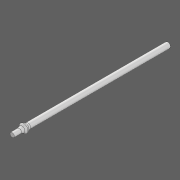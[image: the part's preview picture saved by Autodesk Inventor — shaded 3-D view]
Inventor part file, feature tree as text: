
AUTODESK INVENTOR PART (.ipt)
format: ipt  version: 2020 (Build 240168000, 168)  size: 101,888 bytes
history: native  units: in
note: dims shown in document units (in); Inventor stores cm internally (conversion verified against a paired STEP export)
features: revolve x1, fillet x1, sketch x1
ambient origin geometry x8: Origin, YZ Plane, XZ Plane, XY Plane, X Axis, Y Axis, Z Axis, Center Point
bodies: Solid1 (feature_tree)
feature tree (3):
  revolve  "Revolution1"  [1 undecoded]
  fillet  "Fillet2"  Radius=0.1969in
  sketch  "Sketch1"  dims[d0=90.0deg d5=7.0866in d8=0.1969in d12=0.2362in d14=0.3937in d15=0.2756in d16=0.1969in d17=0.1969in]
note: 1 required parameter value undecoded (feature->parameter linkage not recoverable at this tier; creation-order binding heuristic only, values carry confidence <= 0.55)
